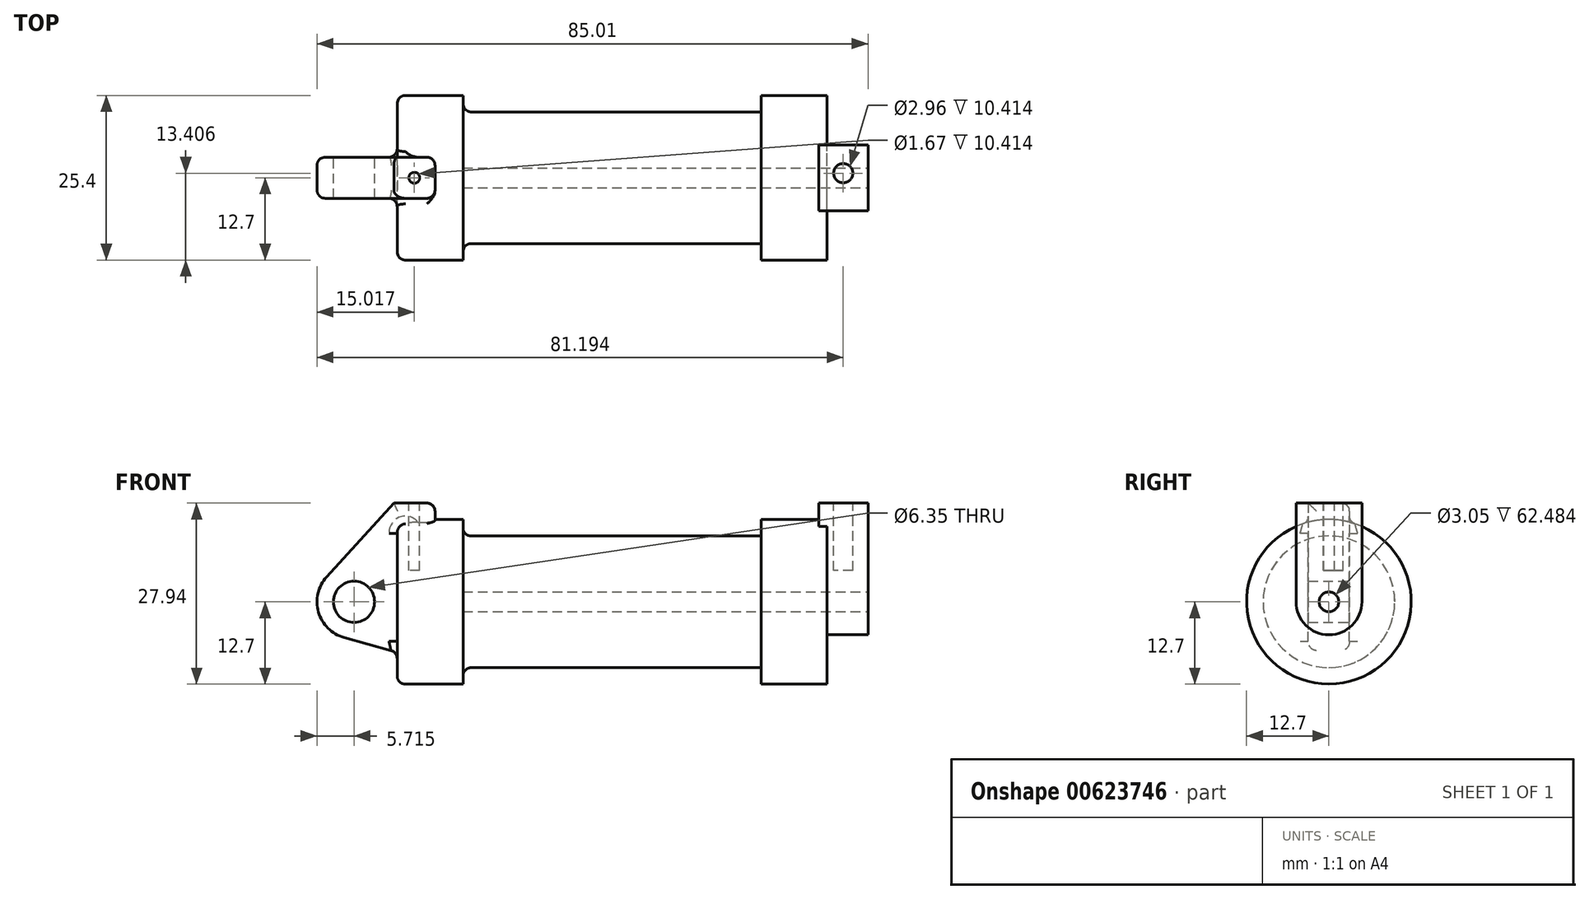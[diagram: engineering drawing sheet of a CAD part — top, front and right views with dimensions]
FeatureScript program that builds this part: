
annotation { "Feature Type Name" : "Feature", "Feature Type Description" : "" }
export const myFeature = defineFeature(function(context is Context, id is Id, definition is map)
    precondition{}
    {
        {
            var Q0;
            Q0=qCreatedBy(makeId("Front.planeOp"),FACE);
            var sketch = newSketch(context, id + "F0", { "sketchPlane" : qUnion([Q0])});
            skLineSegment(sketch, "E0", {"start": v(0, 0) * mm, "end": v(0, 12.7) * mm});
            skLineSegment(sketch, "E1", {"start": v(0, 12.7) * mm, "end": v(10.16, 12.7) * mm});
            skLineSegment(sketch, "E2", {"start": v(10.16, 12.7) * mm, "end": v(10.16, 10.16) * mm});
            skLineSegment(sketch, "E3", {"start": v(10.16, 10.16) * mm, "end": v(56.13, 10.16) * mm});
            skLineSegment(sketch, "E4", {"start": v(56.13, 10.16) * mm, "end": v(56.13, 12.7) * mm});
            skLineSegment(sketch, "E5", {"start": v(56.13, 12.7) * mm, "end": v(66.3, 12.7) * mm});
            skLineSegment(sketch, "E6", {"start": v(66.3, 12.7) * mm, "end": v(66.3, 0) * mm});
            skLineSegment(sketch, "E7", {"start": v(66.3, 0) * mm, "end": v(0, 0) * mm});
            skLineSegment(sketch, "E8", {"start": v(5.84, 15.24) * mm, "end": v(-0.5, 15.24) * mm});
            skLineSegment(sketch, "E9", {"start": v(-0.5, 15.24) * mm, "end": v(-10.88, 3.85) * mm});
            skLineSegment(sketch, "E10", {"start": v(0, 0) * mm, "end": v(-6.65, 0) * mm});
            skCircle(sketch, "E11", {"center": v(-6.65, 0) * mm, "radius": 5.72 * mm});
            skCircle(sketch, "E12", {"center": v(-6.65, 0) * mm, "radius": 3.18 * mm});
            skLineSegment(sketch, "E13", {"start": v(5.84, 15.24) * mm, "end": v(5.84, -9.4) * mm});
            skLineSegment(sketch, "E14", {"start": v(5.84, -9.4) * mm, "end": v(-8.18, -5.5) * mm});
            skSolve(sketch);
        }
        {
            var Q0;
            {var subQ0=sQuery(id+"F0.wireOp",EDGE,"E0");Q0=makeQuery(id+"F0.imprint","IMPRINT",FACE,{"disambiguationData":[TD([[makeQuery(id+"F0.imprint","IMPRINT",EDGE,{"derivedFrom":subQ0}),-1.0]])]});}
            var Q1;
            {var subQ1=sQuery(id+"F0.wireOp",EDGE,"E0");Q1=makeQuery(id+"F0.imprint","IMPRINT",FACE,{"disambiguationData":[TD([[makeQuery(id+"F0.imprint","IMPRINT",EDGE,{"derivedFrom":subQ1}),1.0]])]});}
            var Q2;
            {var subQ5=sQuery(id+"F0.wireOp",EDGE,"E12");Q2=makeQuery(id+"F0.imprint","IMPRINT",FACE,{"disambiguationData":[TD([[makeQuery(id+"F0.imprint","IMPRINT",EDGE,{"derivedFrom":subQ5}),-1.0]])]});}
            var Q3;
            {var subQ0=sQuery(id+"F0.wireOp",EDGE,"E14");Q3=makeQuery(id+"F0.imprint","IMPRINT",FACE,{"disambiguationData":[TD([[makeQuery(id+"F0.imprint","IMPRINT",EDGE,{"derivedFrom":subQ0}),-1.0]])]});}
            extrude(context, id + "F1", {"entities" : qUnion([Q0, Q1, Q2, Q3]), "endBound" : BoundingType.SYMMETRIC, "depth" : 6.35 * mm, "offsetDistance" : 25.4 * mm});
        }
        {
            var Q0;
            {var subQ0=sQuery(id+"F0.wireOp",EDGE,"E2");Q0=makeQuery(id+"F0.imprint","IMPRINT",FACE,{"disambiguationData":[TD([[makeQuery(id+"F0.imprint","IMPRINT",EDGE,{"derivedFrom":subQ0}),-1.0]])]});}
            var Q1;
            {var subQ0=sQuery(id+"F0.wireOp",EDGE,"E0");Q1=makeQuery(id+"F0.imprint","IMPRINT",FACE,{"disambiguationData":[TD([[makeQuery(id+"F0.imprint","IMPRINT",EDGE,{"derivedFrom":subQ0}),-1.0]])]});}
            var Q2;
            Q2=sQuery(id+"F0.wireOp",EDGE,"E7");
            revolve(context, id + "F2", {"operationType" : NewBodyOperationType.ADD, "entities" : qUnion([Q0, Q1]), "axis" : qUnion([Q2]), "revolveType" : RevolveType.FULL});
        }
        {
            var Q0;
            Q0=makeQuery(id+"F2.opRevolve","SWEPT_FACE",FACE,{"disambiguationData":[OSD([sQuery(id+"F0.wireOp",EDGE,"E6")])]});
            var sketch = newSketch(context, id + "F3", { "sketchPlane" : qUnion([Q0])});
            skCircle(sketch, "E15", {"center": v(0, 0) * mm, "radius": 1.52 * mm});
            skCircle(sketch, "E16", {"center": v(0, 0) * mm, "radius": 5.08 * mm});
            skLineSegment(sketch, "E17", {"start": v(5.08, 0) * mm, "end": v(5.08, 15.24) * mm});
            skLineSegment(sketch, "E18.MirrorCS", {"start": v(-5.08, 0) * mm, "end": v(-5.08, 15.24) * mm});
            skLineSegment(sketch, "E19", {"start": v(-5.08, 15.24) * mm, "end": v(5.08, 15.24) * mm});
            skSolve(sketch);
        }
        {
            var Q0;
            {var subQ0=sQuery(id+"F3.wireOp",EDGE,"E19");Q0=makeQuery(id+"F3.imprint","IMPRINT",FACE,{"disambiguationData":[TD([[makeQuery(id+"F3.imprint","IMPRINT",EDGE,{"derivedFrom":subQ0}),-1.0]])]});}
            extrude(context, id + "F4", {"entities" : qUnion([Q0]), "operationType" : NewBodyOperationType.ADD, "oppositeDirection" : true, "depth" : 1.27 * mm, "offsetDistance" : 25.4 * mm});
        }
        {
            var Q0;
            Q0=makeQuery(id+"F3.imprint","IMPRINT",FACE,{"disambiguationData":[TD([[makeQuery(id+"F3.imprint","IMPRINT",EDGE,{"derivedFrom":sQuery(id+"F3.wireOp",EDGE,"E15")}),1.0]])]});
            var Q1;
            Q1=makeQuery(id+"F2.opRevolve","SWEPT_FACE",FACE,{"disambiguationData":[OSD([sQuery(id+"F0.wireOp",EDGE,"E2")])]});
            extrude(context, id + "F5", {"entities" : qUnion([Q0]), "operationType" : NewBodyOperationType.REMOVE, "endBound" : BoundingType.UP_TO_SURFACE, "oppositeDirection" : true, "depth" : 25.4 * mm, "endBoundEntityFace" : qUnion([Q1]), "offsetDistance" : 25.4 * mm});
        }
        {
            var Q0;
            {var subQ0=sQuery(id+"F3.wireOp",EDGE,"E19");Q0=makeQuery(id+"F3.imprint","IMPRINT",FACE,{"disambiguationData":[TD([[makeQuery(id+"F3.imprint","IMPRINT",EDGE,{"derivedFrom":subQ0}),-1.0]])]});}
            var Q1;
            {var subQ0=sQuery(id+"F3.wireOp",EDGE,"E17");var subQ1=sQuery(id+"F3.wireOp",EDGE,"E16");var subQ2=makeQuery(id+"F3.imprint","INTERSECT",VERTEX,{"derivedFrom":[subQ1,subQ0]});Q1=makeQuery(id+"F3.imprint","IMPRINT",FACE,{"disambiguationData":[TD([[makeQuery(id+"F3.imprint","IMPRINT",EDGE,{"disambiguationData":[TD([[subQ2,-1.0]])],"derivedFrom":subQ1}),-1.0]])]});}
            var Q2;
            Q2=makeQuery(id+"F3.imprint","IMPRINT",FACE,{"disambiguationData":[TD([[makeQuery(id+"F3.imprint","IMPRINT",EDGE,{"derivedFrom":sQuery(id+"F3.wireOp",EDGE,"E15")}),-1.0]])]});
            extrude(context, id + "F6", {"entities" : qUnion([Q0, Q1, Q2]), "operationType" : NewBodyOperationType.ADD, "depth" : 6.35 * mm, "offsetDistance" : 25.4 * mm});
        }
        {
            var Q0;
            {var subQ0=sQuery(id+"F3.wireOp",EDGE,"E19");Q0=makeQuery(id+"F6.boolean.opBoolean","MERGE",FACE,{"derivedFrom":[makeQuery(id+"F4.opExtrude","SWEPT_FACE",FACE,{"disambiguationData":[OSD([subQ0])]}),makeQuery(id+"F6.opExtrude","SWEPT_FACE",FACE,{"disambiguationData":[OSD([subQ0])]})]});}
            var sketch = newSketch(context, id + "F7", { "sketchPlane" : qUnion([Q0])});
            skCircle(sketch, "E20", {"center": v(68.82, 0.7) * mm, "radius": 1.48 * mm});
            skSolve(sketch);
        }
        {
            var Q0;
            Q0=makeQuery(id+"F7.imprint","IMPRINT",FACE,{"disambiguationData":[TD([[makeQuery(id+"F7.imprint","IMPRINT",EDGE,{"derivedFrom":sQuery(id+"F7.wireOp",EDGE,"E20")}),1.0]])]});
            extrude(context, id + "F8", {"entities" : qUnion([Q0]), "operationType" : NewBodyOperationType.REMOVE, "oppositeDirection" : true, "depth" : 10.4 * mm, "offsetDistance" : 25.4 * mm});
        }
        {
            var Q0;
            Q0=makeQuery(id+"F1.opExtrude","SWEPT_FACE",FACE,{"disambiguationData":[OSD([sQuery(id+"F0.wireOp",EDGE,"E8")])]});
            var sketch = newSketch(context, id + "F9", { "sketchPlane" : qUnion([Q0])});
            skCircle(sketch, "E21", {"center": v(2.65, 0) * mm, "radius": 0.84 * mm});
            skPoint(sketch, "E21.centerSnap0", {"position": v(-0.5, 0) * mm});
            skSolve(sketch);
        }
        {
            var Q0;
            Q0=makeQuery(id+"F9.imprint","IMPRINT",FACE,{"disambiguationData":[TD([[makeQuery(id+"F9.imprint","IMPRINT",EDGE,{"derivedFrom":sQuery(id+"F9.wireOp",EDGE,"E21")}),1.0]])]});
            extrude(context, id + "F10", {"entities" : qUnion([Q0]), "operationType" : NewBodyOperationType.REMOVE, "oppositeDirection" : true, "depth" : 10.4 * mm, "offsetDistance" : 25.4 * mm});
        }
        {
            var Q0;
            Q0=makeQuery(id+"F2.opRevolve","SWEPT_EDGE",EDGE,{"disambiguationData":[OSD([sQuery(id+"F0.wireOp",EDGE,"E2"),sQuery(id+"F0.wireOp",EDGE,"E3")])]});
            var Q1;
            Q1=makeQuery(id+"F2.boolean.opBoolean","INTERSECT",EDGE,{"derivedFrom":[makeQuery(id+"F1.opExtrude","CAP_FACE",FACE,{"disambiguationData":[OSD([sQuery(id+"F0.wireOp",EDGE,"E8"),sQuery(id+"F0.wireOp",EDGE,"E9"),sQuery(id+"F0.wireOp",EDGE,"E11"),sQuery(id+"F0.wireOp",EDGE,"E12"),sQuery(id+"F0.wireOp",EDGE,"E13"),sQuery(id+"F0.wireOp",EDGE,"E14")])],"isStart":false}),makeQuery(id+"F2.opRevolve","SWEPT_FACE",FACE,{"disambiguationData":[OSD([sQuery(id+"F0.wireOp",EDGE,"E1")])]})]});
            fillet(context, id + "F11", {"entities" : qUnion([Q0, Q1]), "radius" : 1.27 * mm, "tangentPropagation" : true, "allowEdgeOverflow" : false});
        }
        {
            var Q0;
            Q0=makeQuery(id+"F2.boolean.opBoolean","INTERSECT",EDGE,{"derivedFrom":[makeQuery(id+"F1.opExtrude","CAP_FACE",FACE,{"disambiguationData":[OSD([sQuery(id+"F0.wireOp",EDGE,"E8"),sQuery(id+"F0.wireOp",EDGE,"E9"),sQuery(id+"F0.wireOp",EDGE,"E11"),sQuery(id+"F0.wireOp",EDGE,"E12"),sQuery(id+"F0.wireOp",EDGE,"E13"),sQuery(id+"F0.wireOp",EDGE,"E14")])],"isStart":false}),makeQuery(id+"F2.opRevolve","SWEPT_FACE",FACE,{"disambiguationData":[OSD([sQuery(id+"F0.wireOp",EDGE,"E0")])]})]});
            var Q1;
            Q1=makeQuery(id+"F2.opRevolve","SWEPT_EDGE",EDGE,{"disambiguationData":[OSD([sQuery(id+"F0.wireOp",EDGE,"E0"),sQuery(id+"F0.wireOp",EDGE,"E1")])]});
            var Q2;
            Q2=makeQuery(id+"F2.boolean.opBoolean","INTERSECT",EDGE,{"derivedFrom":[makeQuery(id+"F1.opExtrude","CAP_FACE",FACE,{"disambiguationData":[OSD([sQuery(id+"F0.wireOp",EDGE,"E8"),sQuery(id+"F0.wireOp",EDGE,"E9"),sQuery(id+"F0.wireOp",EDGE,"E11"),sQuery(id+"F0.wireOp",EDGE,"E12"),sQuery(id+"F0.wireOp",EDGE,"E13"),sQuery(id+"F0.wireOp",EDGE,"E14")])],"isStart":true}),makeQuery(id+"F2.opRevolve","SWEPT_FACE",FACE,{"disambiguationData":[OSD([sQuery(id+"F0.wireOp",EDGE,"E0")])]})]});
            var Q3;
            Q3=makeQuery(id+"F2.boolean.opBoolean","INTERSECT",EDGE,{"derivedFrom":[makeQuery(id+"F1.opExtrude","SWEPT_FACE",FACE,{"disambiguationData":[OSD([sQuery(id+"F0.wireOp",EDGE,"E14")])]}),makeQuery(id+"F2.opRevolve","SWEPT_FACE",FACE,{"disambiguationData":[OSD([sQuery(id+"F0.wireOp",EDGE,"E0")])]})]});
            var Q4;
            Q4=makeQuery(id+"F1.opExtrude","CAP_EDGE",EDGE,{"disambiguationData":[OSD([sQuery(id+"F0.wireOp",EDGE,"E9")])],"isStart":true});
            var Q5;
            Q5=makeQuery(id+"F1.opExtrude","CAP_EDGE",EDGE,{"disambiguationData":[OSD([sQuery(id+"F0.wireOp",EDGE,"E8")])],"isStart":true});
            var Q6;
            Q6=makeQuery(id+"F1.opExtrude","CAP_EDGE",EDGE,{"disambiguationData":[OSD([sQuery(id+"F0.wireOp",EDGE,"E11")])],"isStart":true});
            var Q7;
            Q7=makeQuery(id+"F1.opExtrude","CAP_EDGE",EDGE,{"disambiguationData":[OSD([sQuery(id+"F0.wireOp",EDGE,"E9")])],"isStart":false});
            var Q8;
            Q8=makeQuery(id+"F1.opExtrude","CAP_EDGE",EDGE,{"disambiguationData":[OSD([sQuery(id+"F0.wireOp",EDGE,"E11")])],"isStart":false});
            var Q9;
            Q9=makeQuery(id+"F1.opExtrude","CAP_EDGE",EDGE,{"disambiguationData":[OSD([sQuery(id+"F0.wireOp",EDGE,"E14")])],"isStart":false});
            fillet(context, id + "F12", {"entities" : qUnion([Q0, Q1, Q2, Q3, Q4, Q5, Q6, Q7, Q8, Q9]), "radius" : 1.27 * mm, "tangentPropagation" : true, "allowEdgeOverflow" : false});
        }
        {
            var Q0;
            Q0=makeQuery(id+"F12.opFillet","BLEND_EDGE",EDGE,{"blendedFrom":[makeQuery(id+"F1.opExtrude","CAP_EDGE",EDGE,{"disambiguationData":[OSD([sQuery(id+"F0.wireOp",EDGE,"E8")])],"isStart":true}),makeQuery(id+"F1.opExtrude","SWEPT_FACE",FACE,{"disambiguationData":[OSD([sQuery(id+"F0.wireOp",EDGE,"E13")])]})],"blendedInto":[makeQuery(id+"F1.opExtrude","SWEPT_FACE",FACE,{"disambiguationData":[OSD([sQuery(id+"F0.wireOp",EDGE,"E13")])]})]});
            var Q1;
            Q1=makeQuery(id+"F1.opExtrude","SWEPT_EDGE",EDGE,{"disambiguationData":[OSD([sQuery(id+"F0.wireOp",EDGE,"E8"),sQuery(id+"F0.wireOp",EDGE,"E13")])]});
            var Q2;
            Q2=makeQuery(id+"F1.opExtrude","CAP_EDGE",EDGE,{"disambiguationData":[OSD([sQuery(id+"F0.wireOp",EDGE,"E13")])],"isStart":false});
            fillet(context, id + "F13", {"entities" : qUnion([Q0, Q1, Q2]), "radius" : 1.27 * mm, "tangentPropagation" : true, "allowEdgeOverflow" : false});
        }
    });
